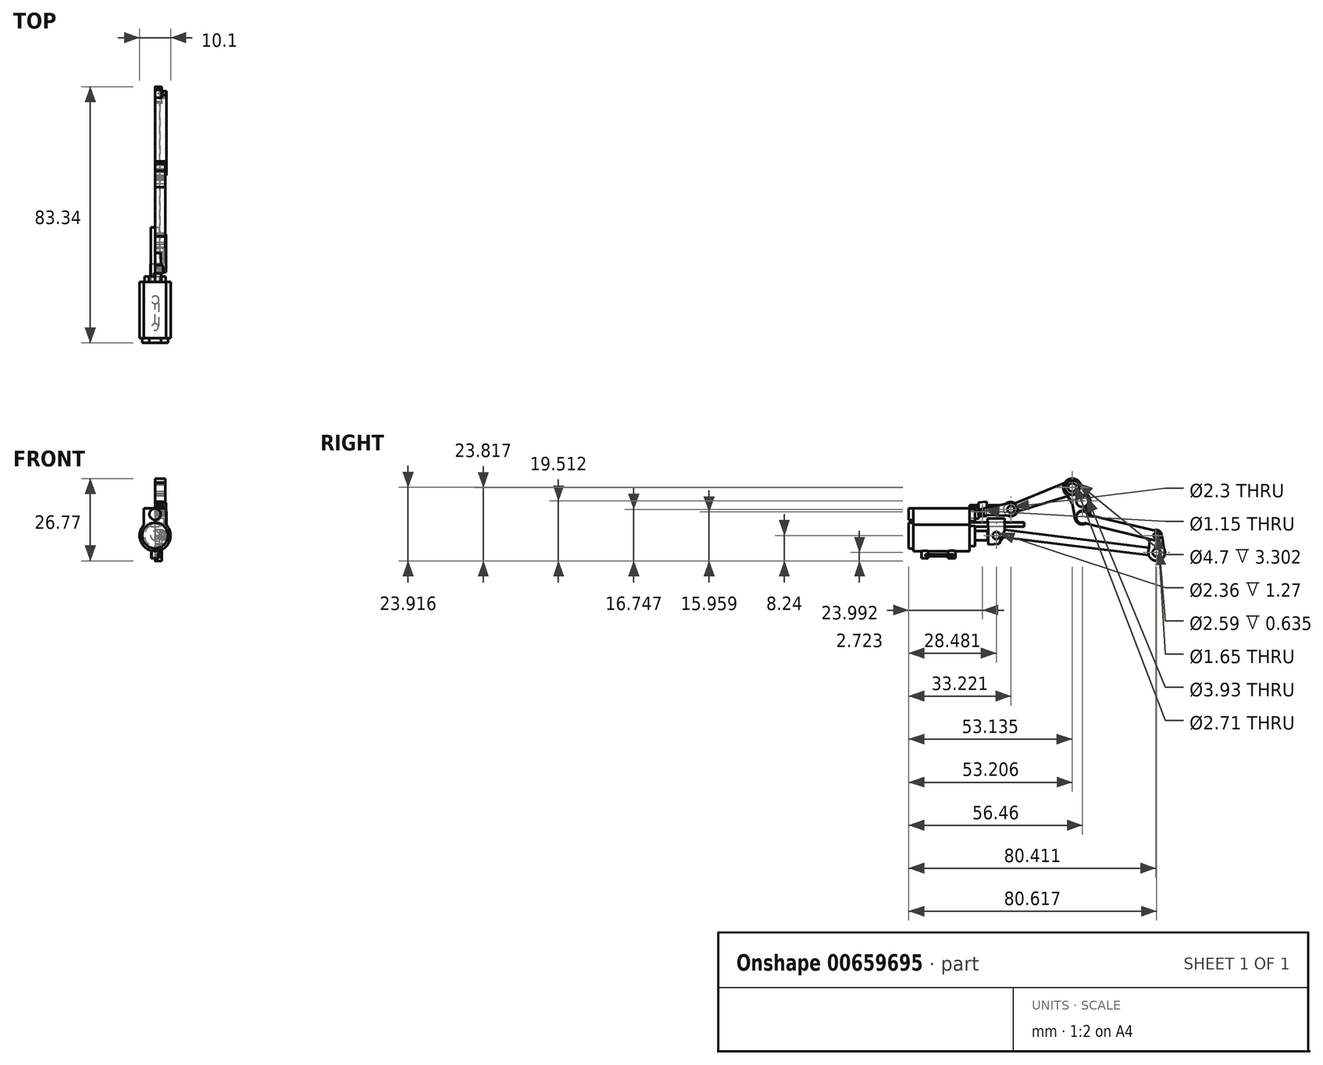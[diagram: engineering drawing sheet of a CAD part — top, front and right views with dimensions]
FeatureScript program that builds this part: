
annotation { "Feature Type Name" : "Feature", "Feature Type Description" : "" }
export const myFeature = defineFeature(function(context is Context, id is Id, definition is map)
    precondition{}
    {
        {
            var Q0;
            Q0=qCreatedBy(makeId("Front.planeOp"),FACE);
            var sketch = newSketch(context, id + "F0", { "sketchPlane" : qUnion([Q0])});
            skCircle(sketch, "E0", {"center": v(0, 0) * mm, "radius": 5.05 * mm});
            skLineSegment(sketch, "E1.bottom", {"start": v(-3.69, 8.87) * mm, "end": v(3.58, 8.87) * mm});
            skLineSegment(sketch, "E1.top", {"start": v(-3.69, 3.57) * mm, "end": v(3.58, 3.57) * mm});
            skLineSegment(sketch, "E1.left", {"start": v(-3.69, 8.87) * mm, "end": v(-3.69, 3.57) * mm});
            skLineSegment(sketch, "E1.right", {"start": v(3.58, 8.87) * mm, "end": v(3.58, 3.57) * mm});
            skSolve(sketch);
        }
        {
            var Q0;
            Q0=qSketchRegion(id+"F0",true);
            extrude(context, id + "F1", {"entities" : qUnion([Q0]), "depth" : 18.29 * mm, "offsetDistance" : 25.4 * mm});
        }
        {
            var Q0;
            Q0=qCreatedBy(makeId("Front.planeOp"),FACE);
            var sketch = newSketch(context, id + "F2", { "sketchPlane" : qUnion([Q0])});
            skCircle(sketch, "E2", {"center": v(0, 0) * mm, "radius": 3.48 * mm});
            skCircle(sketch, "E3", {"center": v(0, 6.69) * mm, "radius": 2.05 * mm});
            skSolve(sketch);
        }
        {
            var Q0;
            Q0=qSketchRegion(id+"F2",true);
            extrude(context, id + "F3", {"entities" : qUnion([Q0]), "operationType" : NewBodyOperationType.ADD, "oppositeDirection" : true, "depth" : 1.78 * mm, "offsetDistance" : 25.4 * mm});
        }
        {
            var Q0;
            Q0=qCreatedBy(makeId("Front.planeOp"),FACE);
            var sketch = newSketch(context, id + "F4", { "sketchPlane" : qUnion([Q0])});
            skCircle(sketch, "E4", {"center": v(0, 0) * mm, "radius": 4.19 * mm});
            skCircle(sketch, "E5", {"center": v(0, 6.96) * mm, "radius": 1.86 * mm});
            skSolve(sketch);
        }
        {
            var Q0;
            Q0=qSketchRegion(id+"F4",true);
            extrude(context, id + "F5", {"entities" : qUnion([Q0]), "operationType" : NewBodyOperationType.ADD, "depth" : 19.8 * mm, "offsetDistance" : 25.4 * mm});
        }
        {
            var Q0;
            Q0=qCreatedBy(makeId("Top.planeOp"),FACE);
            var sketch = newSketch(context, id + "F6", { "sketchPlane" : qUnion([Q0])});
            skCircle(sketch, "E6", {"center": v(0, -14.6) * mm, "radius": 1.06 * mm});
            skCircle(sketch, "E7", {"center": v(0, -5.8) * mm, "radius": 1.24 * mm});
            skSolve(sketch);
        }
        {
            var Q0;
            Q0=qSketchRegion(id+"F6",true);
            extrude(context, id + "F7", {"entities" : qUnion([Q0]), "operationType" : NewBodyOperationType.ADD, "oppositeDirection" : true, "depth" : 7.37 * mm, "offsetDistance" : 25.4 * mm});
        }
        {
            var Q0;
            Q0=qCreatedBy(makeId("Right.planeOp"),FACE);
            var sketch = newSketch(context, id + "F8", { "sketchPlane" : qUnion([Q0])});
            skLineSegment(sketch, "E8.bottom", {"start": v(-14.36, -6.78) * mm, "end": v(-5.2, -6.78) * mm});
            skLineSegment(sketch, "E8.top", {"start": v(-14.36, -6.08) * mm, "end": v(-5.2, -6.08) * mm});
            skLineSegment(sketch, "E8.left", {"start": v(-14.36, -6.78) * mm, "end": v(-14.36, -6.08) * mm});
            skLineSegment(sketch, "E8.right", {"start": v(-5.2, -6.78) * mm, "end": v(-5.2, -6.08) * mm});
            skSolve(sketch);
        }
        {
            var Q0;
            Q0=qSketchRegion(id+"F8",true);
            extrude(context, id + "F9", {"entities" : qUnion([Q0]), "operationType" : NewBodyOperationType.ADD, "depth" : 1.27 * mm, "offsetDistance" : 25.4 * mm});
        }
        {
            var Q0;
            Q0=qCreatedBy(makeId("Front.planeOp"),FACE);
            var sketch = newSketch(context, id + "F10", { "sketchPlane" : qUnion([Q0])});
            skLineSegment(sketch, "E9.bottom", {"start": v(-1.32, 4.33) * mm, "end": v(1.32, 4.33) * mm});
            skLineSegment(sketch, "E9.top", {"start": v(-1.32, 2.91) * mm, "end": v(1.32, 2.91) * mm});
            skLineSegment(sketch, "E9.left", {"start": v(-1.32, 4.33) * mm, "end": v(-1.32, 2.91) * mm});
            skLineSegment(sketch, "E9.right", {"start": v(1.32, 4.33) * mm, "end": v(1.32, 2.91) * mm});
            skPoint(sketch, "E9.middle", {"position": v(0, 3.62) * mm});
            skSolve(sketch);
        }
        {
            var Q0;
            Q0=qSketchRegion(id+"F10",true);
            extrude(context, id + "F11", {"entities" : qUnion([Q0]), "operationType" : NewBodyOperationType.ADD, "oppositeDirection" : true, "depth" : 17.78 * mm, "offsetDistance" : 25.4 * mm});
        }
        {
            var Q0;
            Q0=qCreatedBy(makeId("Right.planeOp"),FACE);
            var sketch = newSketch(context, id + "F12", { "sketchPlane" : qUnion([Q0])});
            skLineSegment(sketch, "E10", {"start": v(5.85, 5.6) * mm, "end": v(11.32, 5.6) * mm});
            skLineSegment(sketch, "E11", {"start": v(11.32, 5.6) * mm, "end": v(11.32, 1.7) * mm});
            skLineSegment(sketch, "E12", {"start": v(11.32, 1.7) * mm, "end": v(6.02, 1.7) * mm});
            skLineSegment(sketch, "E13", {"start": v(6.02, 1.7) * mm, "end": v(5.85, 5.6) * mm});
            skLineSegment(sketch, "E14", {"start": v(6.02, 1.7) * mm, "end": v(6.02, -2.89) * mm});
            skLineSegment(sketch, "E15", {"start": v(11.32, 1.7) * mm, "end": v(9.55, -2.71) * mm});
            skLineSegment(sketch, "E16", {"start": v(9.55, -2.71) * mm, "end": v(6.02, -2.89) * mm});
            skCircle(sketch, "E17", {"center": v(8.67, 0) * mm, "radius": 1.18 * mm});
            skPoint(sketch, "E17.centerSnap0", {"position": v(8.67, 1.7) * mm});
            skSolve(sketch);
        }
        {
            var Q0;
            Q0=qSketchRegion(id+"F12",true);
            extrude(context, id + "F13", {"entities" : qUnion([Q0]), "operationType" : NewBodyOperationType.ADD, "depth" : 2.8 * mm, "offsetDistance" : 25.4 * mm});
        }
        {
            var Q0;
            Q0=qCreatedBy(makeId("Front.planeOp"),FACE);
            var sketch = newSketch(context, id + "F14", { "sketchPlane" : qUnion([Q0])});
            skCircle(sketch, "E18", {"center": v(0, 0) * mm, "radius": 1.49 * mm});
            skSolve(sketch);
        }
        {
            var Q0;
            Q0=qSketchRegion(id+"F14",true);
            extrude(context, id + "F15", {"entities" : qUnion([Q0]), "operationType" : NewBodyOperationType.ADD, "oppositeDirection" : true, "depth" : 5.84 * mm, "offsetDistance" : 25.4 * mm});
        }
        {
            var Q0;
            Q0=qCreatedBy(makeId("Right.planeOp"),FACE);
            var sketch = newSketch(context, id + "F16", { "sketchPlane" : qUnion([Q0])});
            skCircle(sketch, "E19", {"center": v(8.62, 0) * mm, "radius": 2.28 * mm});
            skLineSegment(sketch, "E20", {"start": v(8.62, 2.28) * mm, "end": v(58.69, -3.97) * mm});
            skLineSegment(sketch, "E21", {"start": v(58.69, -3.97) * mm, "end": v(58.38, -6.43) * mm});
            skLineSegment(sketch, "E22", {"start": v(58.38, -6.43) * mm, "end": v(8.62, -0.22) * mm});
            skLineSegment(sketch, "E23", {"start": v(8.62, -0.22) * mm, "end": v(58.38, -6.43) * mm});
            skCircle(sketch, "E24", {"center": v(60.87, -5.6) * mm, "radius": 2.52 * mm});
            skSolve(sketch);
        }
        {
            var Q0;
            Q0 = qSketchRegion(id + "F16", true);
            extrude(context, id + "F17", {"entities" : qUnion([Q0]), "operationType" : NewBodyOperationType.ADD, "depth" : 1.52 * mm, "offsetDistance" : 25.4 * mm});
        }
        {
            var Q0;
            Q0=qCreatedBy(makeId("Right.planeOp"),FACE);
            var sketch = newSketch(context, id + "F18", { "sketchPlane" : qUnion([Q0])});
            skCircle(sketch, "E25", {"center": v(60.8, -5.52) * mm, "radius": 2.72 * mm});
            skCircle(sketch, "E26", {"center": v(60.66, 0) * mm, "radius": 1.84 * mm});
            skLineSegment(sketch, "E27", {"start": v(58.82, 0) * mm, "end": v(58.19, -4.77) * mm});
            skLineSegment(sketch, "E28", {"start": v(62.5, 0) * mm, "end": v(63.25, -4.3) * mm});
            skCircle(sketch, "E29", {"center": v(60.66, 0) * mm, "radius": 1.1 * mm});
            skCircle(sketch, "E30", {"center": v(60.8, -5.52) * mm, "radius": 1.3 * mm});
            skSolve(sketch);
        }
        {
            var Q0;
            Q0 = qSketchRegion(id + "F18", true);
            extrude(context, id + "F19", {"entities" : qUnion([Q0]), "operationType" : NewBodyOperationType.ADD, "depth" : 2.16 * mm, "offsetDistance" : 25.4 * mm});
        }
        {
            var Q0;
            Q0=qCreatedBy(makeId("Right.planeOp"),FACE);
            var sketch = newSketch(context, id + "F20", { "sketchPlane" : qUnion([Q0])});
            skCircle(sketch, "E31", {"center": v(60.6, 0) * mm, "radius": 1.56 * mm});
            skCircle(sketch, "E32", {"center": v(60.6, 0) * mm, "radius": 0.82 * mm});
            skLineSegment(sketch, "E33", {"start": v(61.05, 1.5) * mm, "end": v(38.5, 6.7) * mm});
            skLineSegment(sketch, "E34", {"start": v(60.3, -1.53) * mm, "end": v(37.9, 3.97) * mm});
            skLineSegment(sketch, "E35", {"start": v(37.9, 3.97) * mm, "end": v(38.5, 6.7) * mm});
            skCircle(sketch, "E36", {"center": v(36.73, 5.88) * mm, "radius": 2.03 * mm});
            skSolve(sketch);
        }
        {
            var Q0;
            Q0 = qSketchRegion(id + "F20", true);
            extrude(context, id + "F21", {"entities" : qUnion([Q0]), "operationType" : NewBodyOperationType.ADD, "depth" : 3.7 * mm, "offsetDistance" : 25.4 * mm});
        }
        {
            var Q0;
            Q0=qCreatedBy(makeId("Right.planeOp"),FACE);
            var sketch = newSketch(context, id + "F22", { "sketchPlane" : qUnion([Q0])});
            skCircle(sketch, "E37", {"center": v(36.65, 6.15) * mm, "radius": 2.53 * mm});
            skCircle(sketch, "E38", {"center": v(36.65, 11.27) * mm, "radius": 2.61 * mm});
            skCircle(sketch, "E39", {"center": v(33.4, 15.58) * mm, "radius": 2.95 * mm});
            skLineSegment(sketch, "E40", {"start": v(30.5, 15.03) * mm, "end": v(33.31, 10.53) * mm});
            skLineSegment(sketch, "E41", {"start": v(33.31, 10.53) * mm, "end": v(34.13, 6.4) * mm});
            skLineSegment(sketch, "E42", {"start": v(35.06, 18.01) * mm, "end": v(39, 12.43) * mm});
            skLineSegment(sketch, "E43", {"start": v(39, 12.43) * mm, "end": v(39.18, 6.4) * mm});
            skLineSegment(sketch, "E44", {"start": v(39.18, 11.93) * mm, "end": v(39.18, 6.4) * mm});
            skLineSegment(sketch, "E45", {"start": v(39.18, 11.34) * mm, "end": v(39.18, 6.4) * mm});
            skCircle(sketch, "E46", {"center": v(33.4, 15.58) * mm, "radius": 2.35 * mm});
            skCircle(sketch, "E47", {"center": v(36.65, 11.27) * mm, "radius": 1.96 * mm});
            skCircle(sketch, "E48", {"center": v(36.65, 6.15) * mm, "radius": 1.92 * mm});
            skSolve(sketch);
        }
        {
            var Q0;
            Q0 = qSketchRegion(id + "F22", true);
            extrude(context, id + "F23", {"entities" : qUnion([Q0]), "operationType" : NewBodyOperationType.ADD, "depth" : 3.3 * mm, "offsetDistance" : 25.4 * mm});
        }
        {
            var Q0;
            Q0=qCreatedBy(makeId("Right.planeOp"),FACE);
            var sketch = newSketch(context, id + "F24", { "sketchPlane" : qUnion([Q0])});
            skCircle(sketch, "E49", {"center": v(33.33, 15.68) * mm, "radius": 2.3 * mm});
            skCircle(sketch, "E50", {"center": v(33.33, 15.68) * mm, "radius": 1.36 * mm});
            skLineSegment(sketch, "E51", {"start": v(33.02, 17.97) * mm, "end": v(14.86, 10.58) * mm});
            skLineSegment(sketch, "E52", {"start": v(34.43, 13.65) * mm, "end": v(15.98, 7.96) * mm});
            skLineSegment(sketch, "E53", {"start": v(15.98, 7.96) * mm, "end": v(14.86, 10.58) * mm});
            skCircle(sketch, "E54", {"center": v(13.35, 8.6) * mm, "radius": 2.32 * mm});
            skSolve(sketch);
        }
        {
            var Q0;
            Q0 = qSketchRegion(id + "F24", true);
            extrude(context, id + "F25", {"entities" : qUnion([Q0]), "operationType" : NewBodyOperationType.ADD, "depth" : 3.25 * mm, "offsetDistance" : 25.4 * mm});
        }
        {
            var Q0;
            Q0=qCreatedBy(makeId("Right.planeOp"),FACE);
            var sketch = newSketch(context, id + "F26", { "sketchPlane" : qUnion([Q0])});
            skLineSegment(sketch, "E55.bottom", {"start": v(0, 8.97) * mm, "end": v(9.4, 8.97) * mm});
            skLineSegment(sketch, "E55.top", {"start": v(0, 9.85) * mm, "end": v(9.4, 9.85) * mm});
            skLineSegment(sketch, "E55.left", {"start": v(0, 8.97) * mm, "end": v(0, 9.85) * mm});
            skLineSegment(sketch, "E55.right", {"start": v(9.4, 8.97) * mm, "end": v(9.4, 9.85) * mm});
            skSolve(sketch);
        }
        {
            var Q0;
            Q0 = qSketchRegion(id + "F26", true);
            extrude(context, id + "F27", {"entities" : qUnion([Q0]), "depth" : 1.88 * mm, "offsetDistance" : 25.4 * mm});
        }
        {
            var Q0;
            Q0=qCreatedBy(makeId("Right.planeOp"),FACE);
            var sketch = newSketch(context, id + "F28", { "sketchPlane" : qUnion([Q0])});
            skLineSegment(sketch, "E56", {"start": v(2.86, 10.74) * mm, "end": v(2.86, 6.36) * mm});
            skLineSegment(sketch, "E57", {"start": v(2.86, 6.36) * mm, "end": v(5.49, 6.36) * mm});
            skLineSegment(sketch, "E58", {"start": v(5.49, 6.36) * mm, "end": v(5.49, 10.98) * mm});
            skLineSegment(sketch, "E59", {"start": v(5.49, 10.98) * mm, "end": v(2.86, 10.74) * mm});
            skCircle(sketch, "E60", {"center": v(4.13, 7.8) * mm, "radius": 1.35 * mm});
            skSolve(sketch);
        }
        {
            var Q0;
            Q0 = qSketchRegion(id + "F28", true);
            extrude(context, id + "F29", {"entities" : qUnion([Q0]), "operationType" : NewBodyOperationType.ADD, "depth" : 2.54 * mm, "offsetDistance" : 25.4 * mm});
        }
        {
            var Q0;
            Q0=qCreatedBy(makeId("Front.planeOp"),FACE);
            var sketch = newSketch(context, id + "F30", { "sketchPlane" : qUnion([Q0])});
            skCircle(sketch, "E61", {"center": v(0.78, 6.76) * mm, "radius": 1.2 * mm});
            skSolve(sketch);
        }
        {
            var Q0;
            Q0 = qSketchRegion(id + "F30", true);
            extrude(context, id + "F31", {"entities" : qUnion([Q0]), "oppositeDirection" : true, "depth" : 3 * mm, "offsetDistance" : 25.4 * mm});
        }
        {
            var Q0;
            Q0=qCreatedBy(makeId("Right.planeOp"),FACE);
            var sketch = newSketch(context, id + "F32", { "sketchPlane" : qUnion([Q0])});
            skCircle(sketch, "E62", {"center": v(13.41, 8.5) * mm, "radius": 2.14 * mm});
            skCircle(sketch, "E63", {"center": v(13.41, 8.5) * mm, "radius": 1.15 * mm});
            skCircle(sketch, "E64", {"center": v(4.18, 7.72) * mm, "radius": 1.01 * mm});
            skLineSegment(sketch, "E65", {"start": v(12.84, 10.57) * mm, "end": v(4.18, 8.73) * mm});
            skLineSegment(sketch, "E66", {"start": v(13.85, 6.41) * mm, "end": v(4.18, 6.7) * mm});
            skCircle(sketch, "E67", {"center": v(4.18, 7.72) * mm, "radius": 0.57 * mm});
            skLineSegment(sketch, "E68", {"start": v(4.18, 8.73) * mm, "end": v(4.18, 6.7) * mm});
            skSolve(sketch);
        }
        {
            var Q0;
            Q0 = qSketchRegion(id + "F32", true);
            extrude(context, id + "F33", {"entities" : qUnion([Q0]), "depth" : 3.56 * mm, "offsetDistance" : 25.4 * mm});
        }
    });
